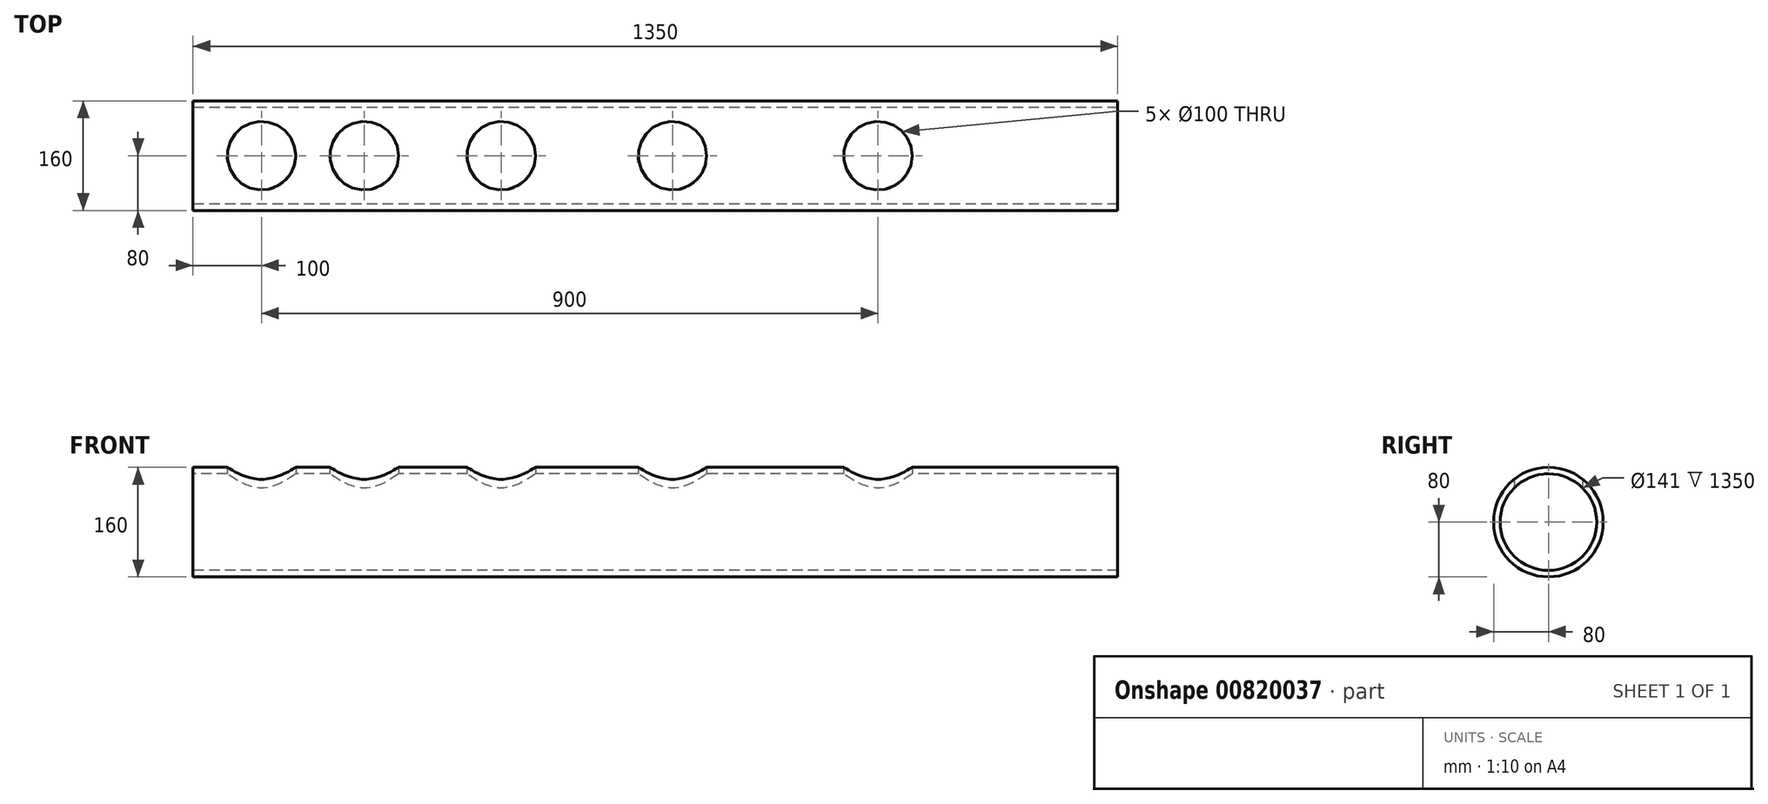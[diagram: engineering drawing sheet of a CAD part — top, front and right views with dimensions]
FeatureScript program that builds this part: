
annotation { "Feature Type Name" : "Feature", "Feature Type Description" : "" }
export const myFeature = defineFeature(function(context is Context, id is Id, definition is map)
    precondition{}
    {
        {
            var Q0;
            Q0=qCreatedBy(makeId("Right.planeOp"),FACE);
            var sketch = newSketch(context, id + "F0", { "sketchPlane" : qUnion([Q0])});
            skCircle(sketch, "E0", {"center": v(0, 0) * mm, "radius": 80 * mm});
            skCircle(sketch, "E1", {"center": v(0, 0) * mm, "radius": 70.5 * mm});
            skSolve(sketch);
        }
        {
            var Q0;
            Q0=qSketchRegion(id+"F0",true);
            extrude(context, id + "F1", {"entities" : qUnion([Q0]), "depth" : 1350 * mm, "offsetDistance" : 25 * mm});
        }
        {
            var Q0;
            Q0=qCreatedBy(makeId("Top.planeOp"),FACE);
            var sketch = newSketch(context, id + "F2", { "sketchPlane" : qUnion([Q0])});
            skLineSegment(sketch, "E2", {"start": v(0, 0) * mm, "end": v(1100, 0) * mm});
            skLineSegment(sketch, "E3", {"start": v(1100, 0) * mm, "end": v(1151.8, -193.18) * mm});
            skLineSegment(sketch, "E4", {"start": v(0, 0) * mm, "end": v(100, 0) * mm});
            skCircle(sketch, "E5", {"center": v(100, 0) * mm, "radius": 50 * mm});
            skLineSegment(sketch, "E6", {"start": v(100, 0) * mm, "end": v(250, 0) * mm});
            skLineSegment(sketch, "E7", {"start": v(250, 0) * mm, "end": v(450, 0) * mm});
            skLineSegment(sketch, "E8", {"start": v(450, 0) * mm, "end": v(700, 0) * mm});
            skLineSegment(sketch, "E9", {"start": v(700, 0) * mm, "end": v(1000, 0) * mm});
            skCircle(sketch, "E10", {"center": v(250, 0) * mm, "radius": 50 * mm});
            skCircle(sketch, "E11", {"center": v(450, 0) * mm, "radius": 50 * mm});
            skCircle(sketch, "E12", {"center": v(700, 0) * mm, "radius": 50 * mm});
            skCircle(sketch, "E13", {"center": v(1000, 0) * mm, "radius": 50 * mm});
            skPoint(sketch, "E14.middle", {"position": v(0, 0) * mm});
            skLineSegment(sketch, "E15", {"start": v(0, 0) * mm, "end": v(0, 130) * mm});
            skLineSegment(sketch, "E16", {"start": v(0, 0) * mm, "end": v(0, -130) * mm});
            skPoint(sketch, "E17.orphan", {"position": v(75, -130) * mm});
            skPoint(sketch, "E18.orphan", {"position": v(75, 130) * mm});
            skArc(sketch, "E19", {"start": v(-35.75, 130) * mm, "mid": v(-50, 0) * mm, "end": v(-35.75, -130) * mm});
            skLineSegment(sketch, "E20", {"start": v(-35.75, 130) * mm, "end": v(0, 130) * mm});
            skLineSegment(sketch, "E21", {"start": v(0, -130) * mm, "end": v(-35.75, -130) * mm});
            skSolve(sketch);
        }
        {
            var Q0;
            {var subQ0=sQuery(id+"F2.wireOp",EDGE,"E6");var subQ1=sQuery(id+"F2.wireOp",EDGE,"E4");var subQ2=makeQuery(id+"F2.imprint","INTERSECT",VERTEX,{"derivedFrom":[subQ1,subQ0]});Q0=makeQuery(id+"F2.imprint","IMPRINT",FACE,{"disambiguationData":[TD([[makeQuery(id+"F2.imprint","IMPRINT",EDGE,{"disambiguationData":[TD([[subQ2,1.0]])],"derivedFrom":subQ1}),-1.0]])]});}
            var Q1;
            {var subQ0=sQuery(id+"F2.wireOp",EDGE,"E6");var subQ1=sQuery(id+"F2.wireOp",EDGE,"E4");var subQ2=makeQuery(id+"F2.imprint","INTERSECT",VERTEX,{"derivedFrom":[subQ1,subQ0]});Q1=makeQuery(id+"F2.imprint","IMPRINT",FACE,{"disambiguationData":[TD([[makeQuery(id+"F2.imprint","IMPRINT",EDGE,{"disambiguationData":[TD([[subQ2,1.0]])],"derivedFrom":subQ1}),1.0]])]});}
            var Q2;
            {var subQ0=sQuery(id+"F2.wireOp",EDGE,"E7");var subQ1=sQuery(id+"F2.wireOp",EDGE,"E6");var subQ2=makeQuery(id+"F2.imprint","INTERSECT",VERTEX,{"derivedFrom":[subQ1,subQ0]});Q2=makeQuery(id+"F2.imprint","IMPRINT",FACE,{"disambiguationData":[TD([[makeQuery(id+"F2.imprint","IMPRINT",EDGE,{"disambiguationData":[TD([[subQ2,1.0]])],"derivedFrom":subQ1}),1.0]])]});}
            var Q3;
            {var subQ0=sQuery(id+"F2.wireOp",EDGE,"E7");var subQ1=sQuery(id+"F2.wireOp",EDGE,"E6");var subQ2=makeQuery(id+"F2.imprint","INTERSECT",VERTEX,{"derivedFrom":[subQ1,subQ0]});Q3=makeQuery(id+"F2.imprint","IMPRINT",FACE,{"disambiguationData":[TD([[makeQuery(id+"F2.imprint","IMPRINT",EDGE,{"disambiguationData":[TD([[subQ2,1.0]])],"derivedFrom":subQ1}),-1.0]])]});}
            var Q4;
            {var subQ0=sQuery(id+"F2.wireOp",EDGE,"E8");var subQ1=sQuery(id+"F2.wireOp",EDGE,"E7");var subQ2=makeQuery(id+"F2.imprint","INTERSECT",VERTEX,{"derivedFrom":[subQ1,subQ0]});Q4=makeQuery(id+"F2.imprint","IMPRINT",FACE,{"disambiguationData":[TD([[makeQuery(id+"F2.imprint","IMPRINT",EDGE,{"disambiguationData":[TD([[subQ2,1.0]])],"derivedFrom":subQ1}),1.0]])]});}
            var Q5;
            {var subQ0=sQuery(id+"F2.wireOp",EDGE,"E8");var subQ1=sQuery(id+"F2.wireOp",EDGE,"E7");var subQ2=makeQuery(id+"F2.imprint","INTERSECT",VERTEX,{"derivedFrom":[subQ1,subQ0]});Q5=makeQuery(id+"F2.imprint","IMPRINT",FACE,{"disambiguationData":[TD([[makeQuery(id+"F2.imprint","IMPRINT",EDGE,{"disambiguationData":[TD([[subQ2,1.0]])],"derivedFrom":subQ1}),-1.0]])]});}
            var Q6;
            {var subQ0=sQuery(id+"F2.wireOp",EDGE,"E9");var subQ1=sQuery(id+"F2.wireOp",EDGE,"E8");var subQ2=makeQuery(id+"F2.imprint","INTERSECT",VERTEX,{"derivedFrom":[subQ1,subQ0]});Q6=makeQuery(id+"F2.imprint","IMPRINT",FACE,{"disambiguationData":[TD([[makeQuery(id+"F2.imprint","IMPRINT",EDGE,{"disambiguationData":[TD([[subQ2,1.0]])],"derivedFrom":subQ1}),1.0]])]});}
            var Q7;
            {var subQ0=sQuery(id+"F2.wireOp",EDGE,"E9");var subQ1=sQuery(id+"F2.wireOp",EDGE,"E8");var subQ2=makeQuery(id+"F2.imprint","INTERSECT",VERTEX,{"derivedFrom":[subQ1,subQ0]});Q7=makeQuery(id+"F2.imprint","IMPRINT",FACE,{"disambiguationData":[TD([[makeQuery(id+"F2.imprint","IMPRINT",EDGE,{"disambiguationData":[TD([[subQ2,1.0]])],"derivedFrom":subQ1}),-1.0]])]});}
            var Q8;
            {var subQ0=sQuery(id+"F2.wireOp",EDGE,"E9");var subQ1=sQuery(id+"F2.wireOp",EDGE,"E2");var subQ2=makeQuery(id+"F2.imprint","INTERSECT",VERTEX,{"derivedFrom":[subQ1,subQ0]});Q8=makeQuery(id+"F2.imprint","IMPRINT",FACE,{"disambiguationData":[TD([[makeQuery(id+"F2.imprint","IMPRINT",EDGE,{"disambiguationData":[TD([[subQ2,-1.0]])],"derivedFrom":subQ1}),1.0]])]});}
            var Q9;
            {var subQ0=sQuery(id+"F2.wireOp",EDGE,"E9");var subQ1=sQuery(id+"F2.wireOp",EDGE,"E2");var subQ2=makeQuery(id+"F2.imprint","INTERSECT",VERTEX,{"derivedFrom":[subQ1,subQ0]});Q9=makeQuery(id+"F2.imprint","IMPRINT",FACE,{"disambiguationData":[TD([[makeQuery(id+"F2.imprint","IMPRINT",EDGE,{"disambiguationData":[TD([[subQ2,-1.0]])],"derivedFrom":subQ1}),-1.0]])]});}
            extrude(context, id + "F3", {"entities" : qUnion([Q0, Q1, Q2, Q3, Q4, Q5, Q6, Q7, Q8, Q9]), "operationType" : NewBodyOperationType.REMOVE, "depth" : 200 * mm, "offsetDistance" : 25 * mm});
        }
    });
